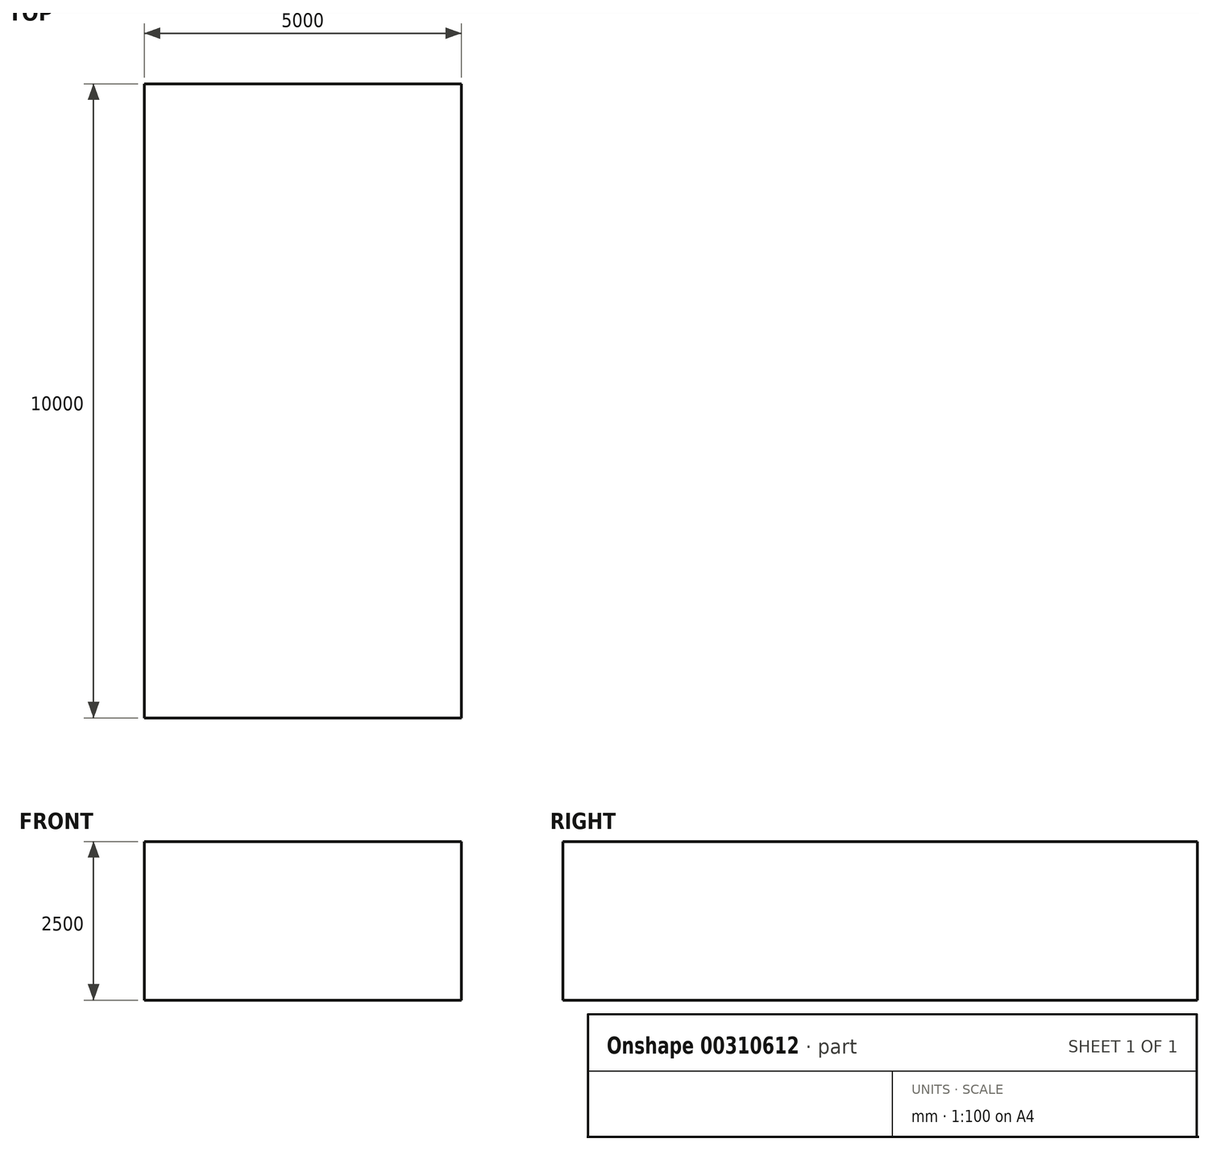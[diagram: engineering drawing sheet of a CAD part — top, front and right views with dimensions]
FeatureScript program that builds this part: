
annotation { "Feature Type Name" : "Feature", "Feature Type Description" : "" }
export const myFeature = defineFeature(function(context is Context, id is Id, definition is map)
    precondition{}
    {
        {
            var Q0;
            Q0=qCreatedBy(makeId("Front.planeOp"),FACE);
            var sketch = newSketch(context, id + "F0", { "sketchPlane" : qUnion([Q0])});
            skLineSegment(sketch, "E0.bottom", {"start": v(0, 0) * mm, "end": v(-5000, 0) * mm});
            skLineSegment(sketch, "E0.top", {"start": v(0, 2500) * mm, "end": v(-5000, 2500) * mm});
            skLineSegment(sketch, "E0.left", {"start": v(0, 0) * mm, "end": v(0, 2500) * mm});
            skLineSegment(sketch, "E0.right", {"start": v(-5000, 0) * mm, "end": v(-5000, 2500) * mm});
            skSolve(sketch);
        }
        {
            var Q0;
            Q0 = qSketchRegion(id + "F0", true);
            extrude(context, id + "F1", {"entities" : qUnion([Q0]), "depth" : 10000 * mm});
        }
    });
